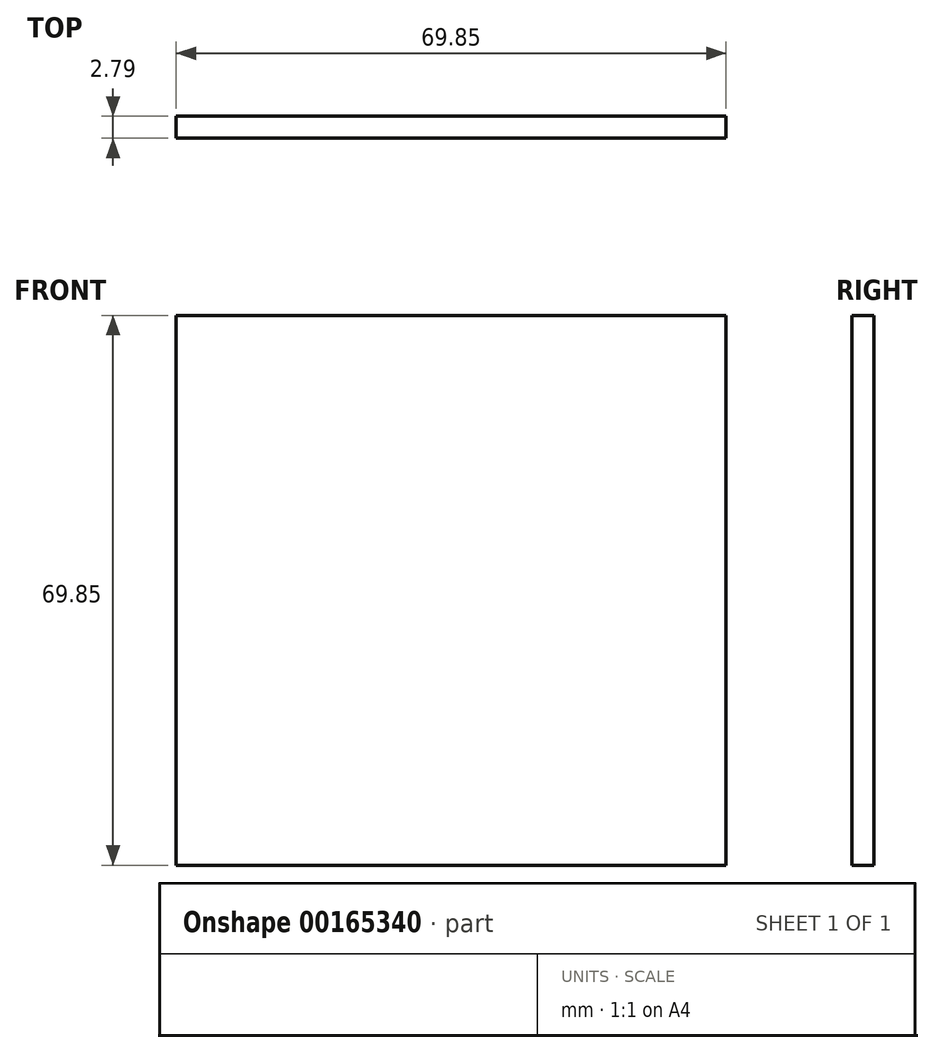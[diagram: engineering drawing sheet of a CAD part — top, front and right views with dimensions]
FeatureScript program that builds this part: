
annotation { "Feature Type Name" : "Feature", "Feature Type Description" : "" }
export const myFeature = defineFeature(function(context is Context, id is Id, definition is map)
    precondition{}
    {
        {
            var Q0;
            Q0=qCreatedBy(makeId("Front.planeOp"),FACE);
            var sketch = newSketch(context, id + "F0", { "sketchPlane" : qUnion([Q0])});
            skLineSegment(sketch, "E0.bottom", {"start": v(-40.5, 36.05) * mm, "end": v(29.35, 36.05) * mm});
            skLineSegment(sketch, "E0.top", {"start": v(-40.5, -33.8) * mm, "end": v(29.35, -33.8) * mm});
            skLineSegment(sketch, "E0.left", {"start": v(-40.5, 36.05) * mm, "end": v(-40.5, -33.8) * mm});
            skLineSegment(sketch, "E0.right", {"start": v(29.35, 36.05) * mm, "end": v(29.35, -33.8) * mm});
            skSolve(sketch);
        }
        {
            var Q0;
            Q0=qSketchRegion(id+"F0",true);
            extrude(context, id + "F1", {"entities" : qUnion([Q0]), "depth" : 2.8 * mm});
        }
    });
